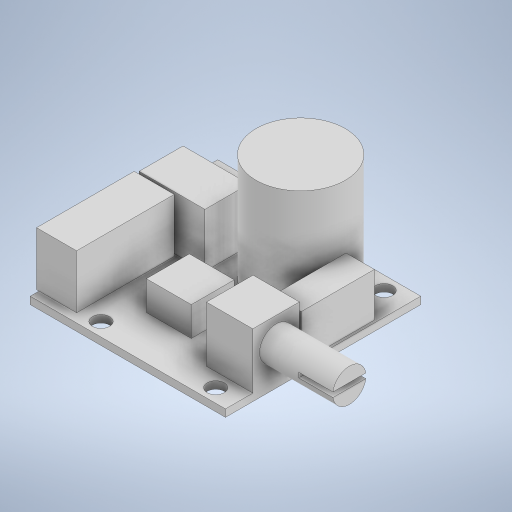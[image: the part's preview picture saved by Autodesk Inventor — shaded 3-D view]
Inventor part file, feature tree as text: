
AUTODESK INVENTOR PART (.ipt)
format: ipt  version: 2023 (Build 270158000, 158)  size: 393,728 bytes
history: native  units: in
note: dims shown in document units (in); Inventor stores cm internally (conversion verified against a paired STEP export)
features: extrude x13, sketch x6, projected_geometry x2
ambient origin geometry x8: Origin, YZ Plane, XZ Plane, XY Plane, X Axis, Y Axis, Z Axis, Center Point
bodies: Solid1 (feature_tree)
feature tree (21):
  extrude  "Extrusion1"  Depth=1.5748in
  sketch  "Sketch2"  dims[d2=0.0591in d3=0.0in d4=0.1378in]
  extrude  "Extrusion2"  Depth=0.0591in
  extrude  "Extrusion3"  Depth=0.1378in
  extrude  "Extrusion4"  Depth=0.7205in
  extrude  "Extrusion5"  Depth=0.7874in
  extrude  "Extrusion6"  Depth=0.3622in
  extrude  "Extrusion7"  Depth=0.376in
  extrude  "Extrusion8"  Depth=0.374in
  extrude  "Extrusion9"  Depth=0.5906in
  extrude  "Extrusion10"  Depth=0.2283in
  extrude  "Extrusion11"  Depth=0.4331in
  extrude  "Extrusion12"  Depth=0.2362in
  extrude  "Extrusion13"  Depth=0.3543in
  sketch  "Sketch1"  dims[d0=1.5748in d1=1.5748in]
  projected_geometry  "Projected Loop1"
  sketch  "Sketch3"  dims[d5=0.1378in d6=0.1378in]
  sketch  "Sketch4"  dims[d7=0.1378in d8=0.7205in]
  sketch  "Sketch5"  dims[d9=0.3228in d10=0.7874in]
  sketch  "Sketch6"  dims[d11=0.3465in d12=0.3622in d13=0.376in d14=0.374in d15=0.5906in d16=0.2283in d17=0.4331in d18=0.2362in d21=0.3543in d22=0.5512in d23=0.2205in d24=0.187in d25=0.1083in d26=0.0197in d27=0.3543in d28=0.3543in d29=0.2559in d30=0.3602in d31=0.3602in d32=0.1083in d33=0.0197in d34=0.0709in d35=0.063in d37=0.0197in d38=0.0197in d39=0.4626in d40=0.1083in d41=0.1083in d42=0.187in d43=0.561in d44=0.2362in d45=0.0in d46=0.8661in d47=0.0in d48=0.0in d49=0.0in d50=0.4331in d51=0.0in d52=0.4488in d53=0.0in d54=0.3543in d55=0.0in d56=0.4331in d57=0.0in d58=0.1969in d59=0.0in d60=0.2461in d61=0.1821in d62=0.5118in d63=0.0in d64=0.1969in d65=0.0394in d66=0.2362in d67=0.1181in d68=0.0984in d69=0.0in d70=0.2677in d71=0.1929in d72=0.188in d73=0.376in d74=0.5906in d75=0.0in d76=0.0394in d77=0.2756in d78=0.0in]
  projected_geometry  "Projected Loop2"
